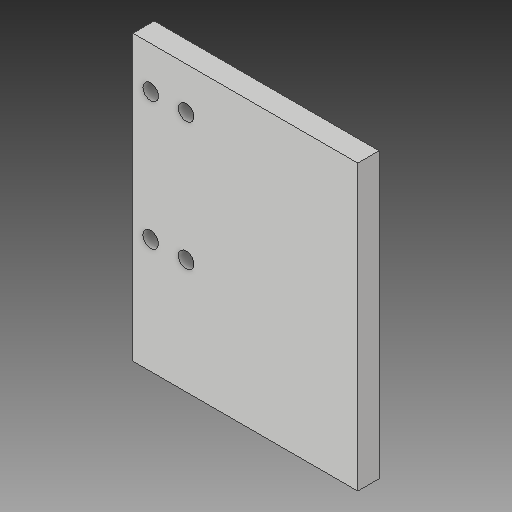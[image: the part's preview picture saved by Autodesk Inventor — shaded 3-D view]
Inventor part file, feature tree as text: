
AUTODESK INVENTOR PART (.ipt)
format: ipt  version: 2018 (Build 220112000, 112)  size: 122,368 bytes
history: native  units: mm
features: reference x4, extrude x3, sketch x3, fillet x1
ambient origin geometry x8: Origin, YZ Plane, XZ Plane, XY Plane, X Axis, Y Axis, Z Axis, Center Point
bodies: Solid1 (feature_tree)
feature tree (11):
  extrude  "Extrusion1"  Depth=95.0mm
  extrude  "Extrusion3"  Depth=7.0mm
  fillet  "Fillet1"  Radius=35.0mm
  extrude  "Extrusion4"  Depth=3.0mm TaperAngle=0.0deg
  sketch  "Sketch1"  dims[d0=120.0mm d1=95.0mm]
  sketch  "Sketch3"  dims[d2=6.0mm d3=0.0mm d9=7.0mm d10=35.0mm]
  sketch  "Sketch4"  dims[d11=75.0mm d12=3.0mm d13=0.0mm d14=7.0mm d15=10.0mm d16=0.0mm]
  reference  "Reference1"
  reference  "Reference2"
  reference  "Reference3"
  reference  "Reference4"
